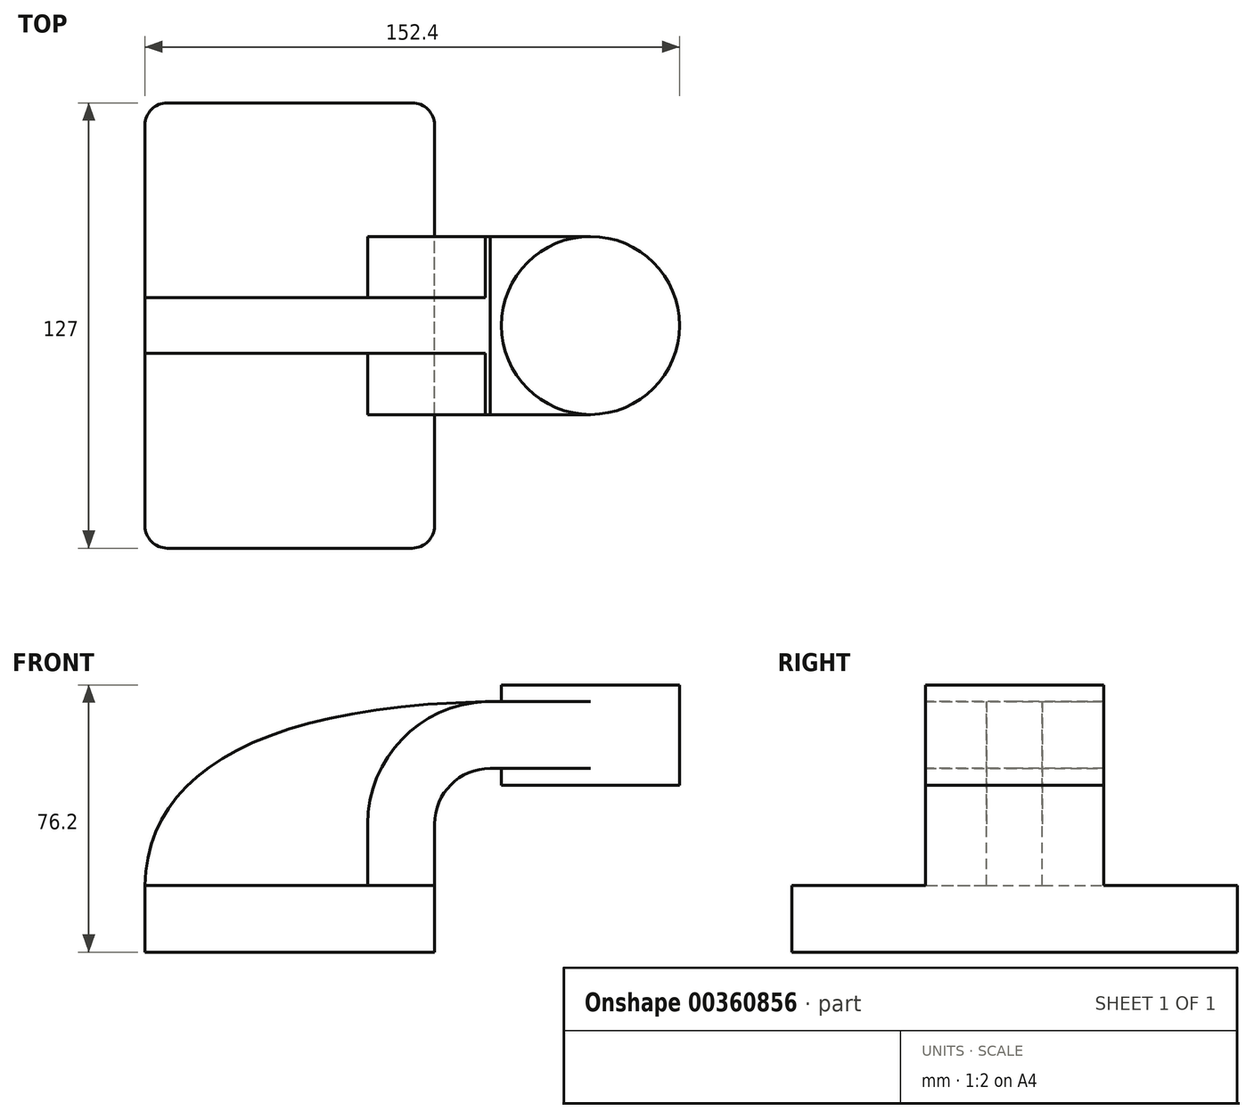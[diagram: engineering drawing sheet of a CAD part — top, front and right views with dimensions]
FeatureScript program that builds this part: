
annotation { "Feature Type Name" : "Feature", "Feature Type Description" : "" }
export const myFeature = defineFeature(function(context is Context, id is Id, definition is map)
    precondition{}
    {
        {
            var Q0;
            Q0=qCreatedBy(makeId("Front.planeOp"),FACE);
            var sketch = newSketch(context, id + "F0", { "sketchPlane" : qUnion([Q0])});
            skLineSegment(sketch, "E0.bottom", {"start": v(50.83, 7.7) * mm, "end": v(-31.72, 7.7) * mm});
            skLineSegment(sketch, "E0.top", {"start": v(50.83, -11.34) * mm, "end": v(-31.72, -11.34) * mm});
            skLineSegment(sketch, "E0.left", {"start": v(50.83, 7.7) * mm, "end": v(50.83, -11.34) * mm});
            skLineSegment(sketch, "E0.right", {"start": v(-31.72, 7.7) * mm, "end": v(-31.72, -11.34) * mm});
            skPoint(sketch, "E0.middle", {"position": v(9.55, -1.82) * mm});
            skLineSegment(sketch, "E1.bottom", {"start": v(120.68, 36.28) * mm, "end": v(69.88, 36.28) * mm});
            skLineSegment(sketch, "E1.top", {"start": v(120.68, 64.86) * mm, "end": v(69.88, 64.86) * mm});
            skLineSegment(sketch, "E1.left", {"start": v(120.68, 36.28) * mm, "end": v(120.68, 64.86) * mm});
            skLineSegment(sketch, "E1.right", {"start": v(69.88, 36.28) * mm, "end": v(69.88, 64.86) * mm});
            skPoint(sketch, "E1.middle", {"position": v(95.28, 50.57) * mm});
            skLineSegment(sketch, "E2", {"start": v(50.83, 7.7) * mm, "end": v(50.83, 25.18) * mm});
            skArc(sketch, "E3", {"start": v(50.83, 25.18) * mm, "mid": v(55.48, 36.4) * mm, "end": v(66.7, 41.06) * mm});
            skLineSegment(sketch, "E4", {"start": v(66.7, 41.06) * mm, "end": v(95.28, 41.06) * mm});
            skLineSegment(sketch, "E5.0", {"start": v(66.7, 60.1) * mm, "end": v(95.28, 60.1) * mm});
            skArc(sketch, "E5.1", {"start": v(31.78, 25.18) * mm, "mid": v(42, 49.88) * mm, "end": v(66.7, 60.1) * mm});
            skLineSegment(sketch, "E5.2", {"start": v(31.78, 7.7) * mm, "end": v(31.78, 25.18) * mm});
            skFitSpline(sketch, "E6", {"points": [v(-31.72, 7.7) * mm, v(66.7, 60.1) * mm], "startDerivative": vector(1.77, 94.18) * mm, "endDerivative": vector(200.1, 3.63) * mm});
            skLineSegment(sketch, "E7", {"start": v(95.28, 36.28) * mm, "end": v(95.28, 64.86) * mm});
            skSolve(sketch);
        }
        {
            var Q0;
            Q0=makeQuery(id+"F0.imprint","IMPRINT",FACE,{"disambiguationData":[TD([[makeQuery(id+"F0.imprint","IMPRINT",EDGE,{"derivedFrom":sQuery(id+"F0.wireOp",EDGE,"E0.top")}),-1.0]])]});
            extrude(context, id + "F1", {"entities" : qUnion([Q0]), "endBound" : BoundingType.SYMMETRIC, "depth" : 127 * mm});
        }
        {
            var Q0;
            {var subQ1=sQuery(id+"F0.wireOp",EDGE,"E2");Q0=makeQuery(id+"F0.imprint","IMPRINT",FACE,{"disambiguationData":[TD([[makeQuery(id+"F0.imprint","IMPRINT",EDGE,{"derivedFrom":subQ1}),1.0]])]});}
            var Q1;
            {var subQ0=sQuery(id+"F0.wireOp",EDGE,"E4");var subQ1=sQuery(id+"F0.wireOp",EDGE,"E1.right");var subQ2=makeQuery(id+"F0.imprint","INTERSECT",VERTEX,{"derivedFrom":[subQ1,subQ0]});Q1=makeQuery(id+"F0.imprint","IMPRINT",FACE,{"disambiguationData":[TD([[makeQuery(id+"F0.imprint","IMPRINT",EDGE,{"disambiguationData":[TD([[subQ2,-1.0]])],"derivedFrom":subQ1}),-1.0]])]});}
            extrude(context, id + "F2", {"entities" : qUnion([Q0, Q1]), "operationType" : NewBodyOperationType.ADD, "endBound" : BoundingType.SYMMETRIC, "depth" : 50.8 * mm});
        }
        {
            var Q0;
            {var subQ3=sQuery(id+"F0.wireOp",EDGE,"E5.2");Q0=makeQuery(id+"F0.imprint","IMPRINT",FACE,{"disambiguationData":[TD([[makeQuery(id+"F0.imprint","IMPRINT",EDGE,{"derivedFrom":subQ3}),1.0]])]});}
            extrude(context, id + "F3", {"entities" : qUnion([Q0]), "operationType" : NewBodyOperationType.ADD, "endBound" : BoundingType.SYMMETRIC, "depth" : 15.88 * mm});
        }
        {
            var Q0;
            {var subQ4=sQuery(id+"F0.wireOp",EDGE,"E1.left");Q0=makeQuery(id+"F0.imprint","IMPRINT",FACE,{"disambiguationData":[TD([[makeQuery(id+"F0.imprint","IMPRINT",EDGE,{"derivedFrom":subQ4}),1.0]])]});}
            var Q1;
            Q1=sQuery(id+"F0.wireOp",EDGE,"E7");
            revolve(context, id + "F4", {"operationType" : NewBodyOperationType.ADD, "entities" : qUnion([Q0]), "axis" : qUnion([Q1]), "revolveType" : RevolveType.FULL});
        }
        {
            var Q0;
            Q0=makeQuery(id+"F1.opExtrude","CAP_EDGE",EDGE,{"disambiguationData":[OSD([sQuery(id+"F0.wireOp",EDGE,"E0.right")])],"isStart":false});
            var Q1;
            Q1=makeQuery(id+"F1.opExtrude","CAP_EDGE",EDGE,{"disambiguationData":[OSD([sQuery(id+"F0.wireOp",EDGE,"E0.left")])],"isStart":false});
            var Q2;
            Q2=makeQuery(id+"F1.opExtrude","CAP_EDGE",EDGE,{"disambiguationData":[OSD([sQuery(id+"F0.wireOp",EDGE,"E0.left")])],"isStart":true});
            var Q3;
            Q3=makeQuery(id+"F1.opExtrude","CAP_EDGE",EDGE,{"disambiguationData":[OSD([sQuery(id+"F0.wireOp",EDGE,"E0.right")])],"isStart":true});
            fillet(context, id + "F5", {"entities" : qUnion([Q0, Q1, Q2, Q3]), "radius" : 6.35 * mm, "tangentPropagation" : true, "allowEdgeOverflow" : false});
        }
    });
